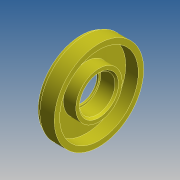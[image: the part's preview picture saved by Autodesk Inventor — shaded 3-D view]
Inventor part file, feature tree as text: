
AUTODESK INVENTOR PART (.ipt)
format: ipt  version: 2015 SP1 (Build 190203100, 203)  size: 230,912 bytes
history: native  units: mm
features: revolve x1, chamfer x1, sketch x1
ambient origin geometry x8: Origin, YZ Plane, XZ Plane, XY Plane, X Axis, Y Axis, Z Axis, Center Point
bodies: Solid1 (feature_tree)
feature tree (3):
  revolve  "Revolution1"  [1 undecoded]
  chamfer  "Chamfer1"  Distance=10.0mm
  sketch  "Sketch1"  dims[d0=49.8mm d1=47.8mm d2=10.0mm d3=1.0mm d4=2.0mm d5=19.8mm d6=1.0mm d7=3.0mm d8=3.0mm d9=3.0mm d10=10.0mm d11=90.0deg d12=1.0mm d13=2.0mm d14=45.0deg]
note: 1 required parameter value undecoded (feature->parameter linkage not recoverable at this tier; creation-order binding heuristic only, values carry confidence <= 0.55)
